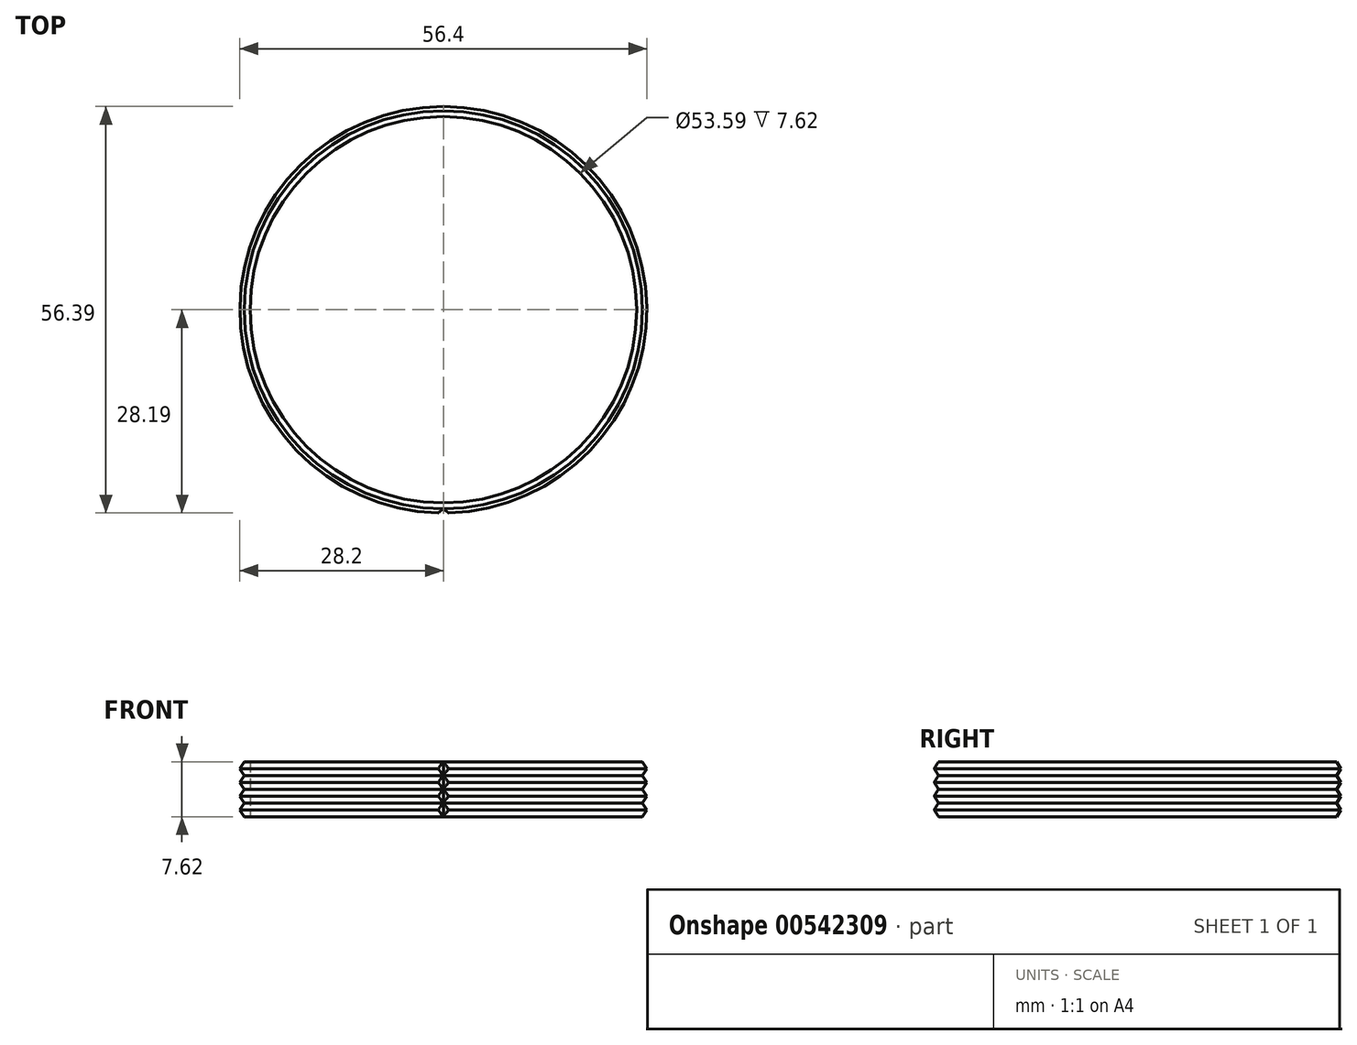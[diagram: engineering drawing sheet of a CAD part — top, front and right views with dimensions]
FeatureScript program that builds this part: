
annotation { "Feature Type Name" : "Feature", "Feature Type Description" : "" }
export const myFeature = defineFeature(function(context is Context, id is Id, definition is map)
    precondition{}
    {
        {
            var Q0;
            Q0=qCreatedBy(makeId("Front.planeOp"),FACE);
            var sketch = newSketch(context, id + "F0", { "sketchPlane" : qUnion([Q0])});
            skLineSegment(sketch, "E0", {"start": v(26.8, 0) * mm, "end": v(26.8, 7.62) * mm});
            skLineSegment(sketch, "E1", {"start": v(26.8, 7.62) * mm, "end": v(27.6, 7.62) * mm});
            skLineSegment(sketch, "E2", {"start": v(27.6, 7.62) * mm, "end": v(27.6, 0) * mm});
            skLineSegment(sketch, "E3", {"start": v(27.6, 0) * mm, "end": v(26.8, 0) * mm});
            skLineSegment(sketch, "E4", {"start": v(0, 0) * mm, "end": v(0, 8.2) * mm, "construction": true});
            skLineSegment(sketch, "E5", {"start": v(27.6, 0) * mm, "end": v(28.2, 0.95) * mm});
            skLineSegment(sketch, "E6", {"start": v(28.2, 0.95) * mm, "end": v(27.6, 1.9) * mm});
            skLineSegment(sketch, "E7", {"start": v(28.2, 0) * mm, "end": v(28.2, 7.59) * mm, "construction": true});
            skLineSegment(sketch, "E8", {"start": v(27.6, 1.9) * mm, "end": v(28.2, 2.86) * mm});
            skLineSegment(sketch, "E9", {"start": v(28.2, 2.86) * mm, "end": v(27.6, 3.8) * mm});
            skLineSegment(sketch, "E10", {"start": v(27.6, 3.8) * mm, "end": v(28.2, 4.76) * mm});
            skLineSegment(sketch, "E11", {"start": v(28.2, 4.76) * mm, "end": v(27.6, 5.72) * mm});
            skLineSegment(sketch, "E12", {"start": v(27.6, 5.72) * mm, "end": v(28.2, 6.67) * mm});
            skLineSegment(sketch, "E13", {"start": v(28.2, 6.67) * mm, "end": v(27.6, 7.62) * mm});
            skSolve(sketch);
        }
        {
            var Q0;
            Q0 = qSketchRegion(id + "F0", true);
            var Q1;
            Q1=sQuery(id+"F0.wireOp",EDGE,"E4");
            revolve(context, id + "F1", {"entities" : qUnion([Q0]), "axis" : qUnion([Q1]), "revolveType" : RevolveType.FULL});
        }
        {
            var Q0;
            Q0=qCreatedBy(makeId("Top.planeOp"),FACE);
            var sketch = newSketch(context, id + "F2", { "sketchPlane" : qUnion([Q0])});
            skPoint(sketch, "E14", {"position": v(0, -27.6) * mm});
            skLineSegment(sketch, "E15", {"start": v(0, -27.6) * mm, "end": v(-0.74, -28.2) * mm});
            skLineSegment(sketch, "E16", {"start": v(-0.74, -28.2) * mm, "end": v(0.74, -28.2) * mm});
            skLineSegment(sketch, "E17", {"start": v(0.74, -28.2) * mm, "end": v(0, -27.6) * mm});
            skPoint(sketch, "E18", {"position": v(0, -28.2) * mm});
            skLineSegment(sketch, "E19", {"start": v(0, 0) * mm, "end": v(-0.74, -28.2) * mm, "construction": true});
            skLineSegment(sketch, "E20", {"start": v(0.74, -28.2) * mm, "end": v(0, 0) * mm, "construction": true});
            skSolve(sketch);
        }
        {
            var Q0;
            Q0 = qSketchRegion(id + "F2", true);
            extrude(context, id + "F3", {"entities" : qUnion([Q0]), "operationType" : NewBodyOperationType.REMOVE, "endBound" : BoundingType.THROUGH_ALL, "depth" : 25.4 * mm, "offsetDistance" : 25.4 * mm});
        }
    });
